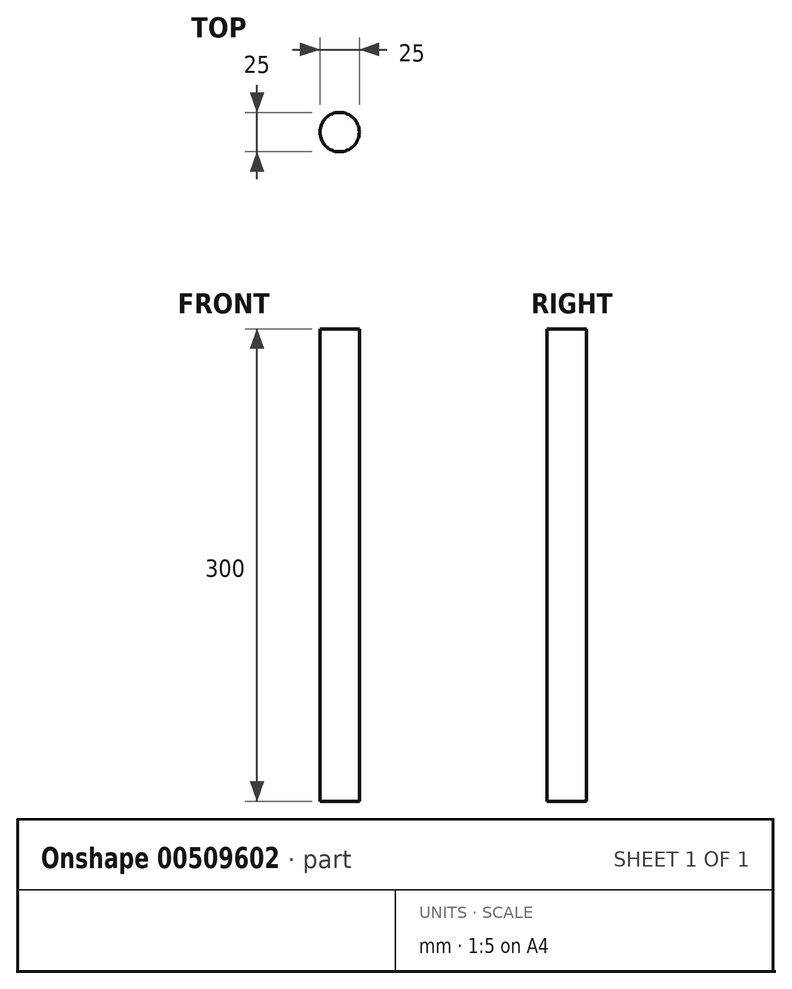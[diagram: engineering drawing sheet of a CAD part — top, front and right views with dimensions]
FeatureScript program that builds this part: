
annotation { "Feature Type Name" : "Feature", "Feature Type Description" : "" }
export const myFeature = defineFeature(function(context is Context, id is Id, definition is map)
    precondition{}
    {
        {
            var Q0;
            Q0=qCreatedBy(makeId("Top.planeOp"),FACE);
            var sketch = newSketch(context, id + "F0", { "sketchPlane" : qUnion([Q0])});
            skCircle(sketch, "E0", {"center": v(0, 0) * mm, "radius": 12.5 * mm});
            skSolve(sketch);
        }
        {
            var Q0;
            Q0=makeQuery(id+"F0.imprint","IMPRINT",FACE,{"disambiguationData":[TD([[makeQuery(id+"F0.imprint","IMPRINT",EDGE,{"derivedFrom":sQuery(id+"F0.wireOp",EDGE,"E0")}),1.0]])]});
            extrude(context, id + "F1", {"entities" : qUnion([Q0]), "endBound" : BoundingType.SYMMETRIC, "depth" : 300 * mm, "offsetDistance" : 25 * mm});
        }
    });
